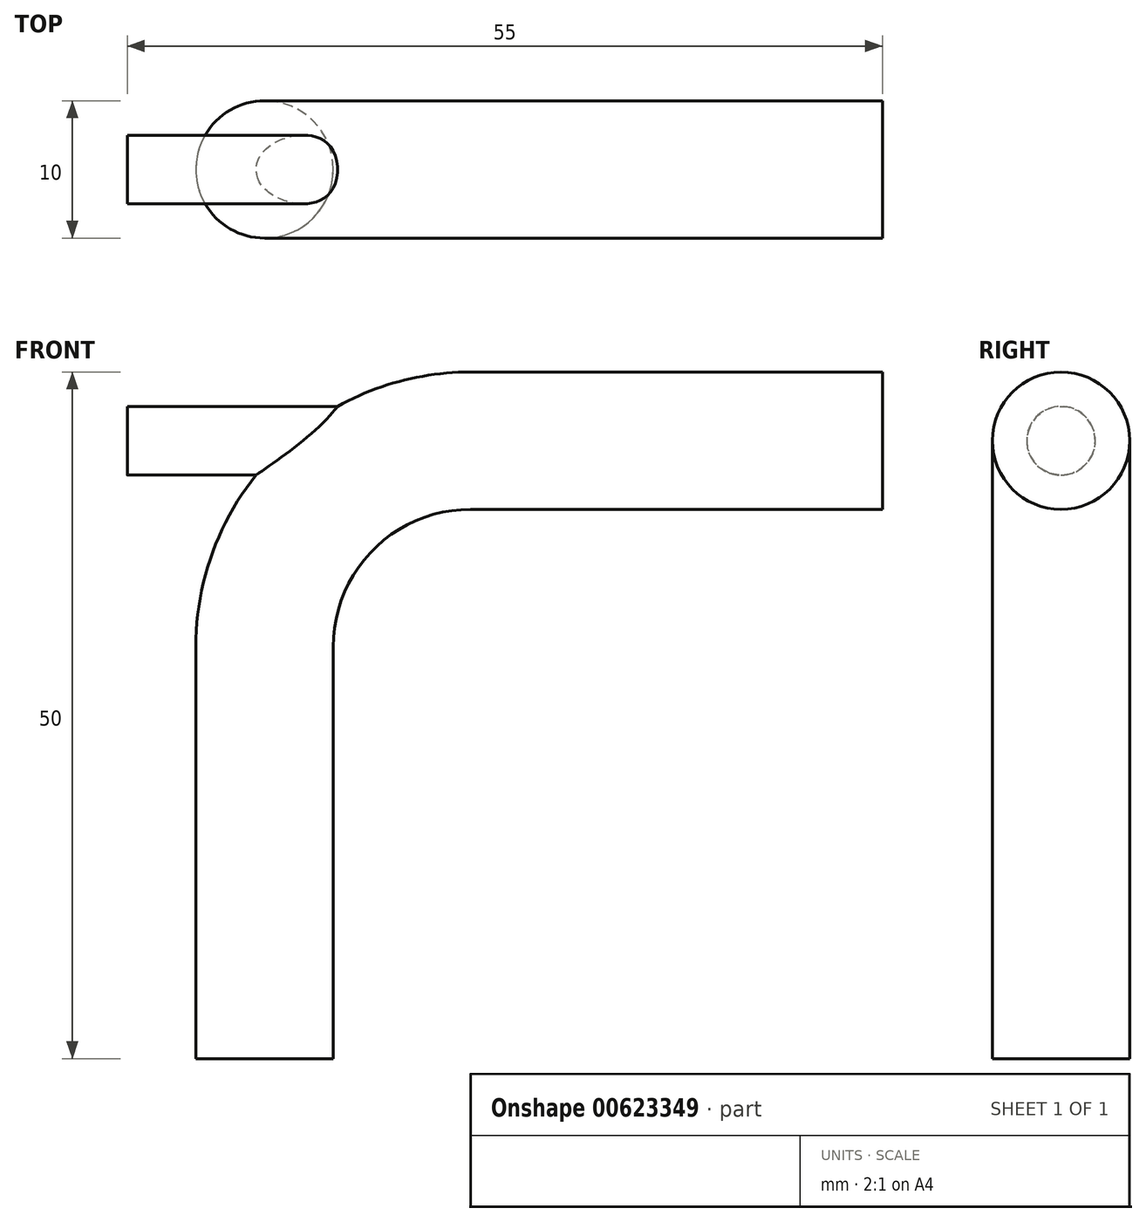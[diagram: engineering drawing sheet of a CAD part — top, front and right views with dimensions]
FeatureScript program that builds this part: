
annotation { "Feature Type Name" : "Feature", "Feature Type Description" : "" }
export const myFeature = defineFeature(function(context is Context, id is Id, definition is map)
    precondition{}
    {
        {
            var Q0;
            Q0=qCreatedBy(makeId("Front.planeOp"),FACE);
            var sketch = newSketch(context, id + "F0", { "sketchPlane" : qUnion([Q0])});
            skLineSegment(sketch, "E0", {"start": v(0, 0) * mm, "end": v(0, 30) * mm});
            skArc(sketch, "E1", {"start": v(15, 45) * mm, "mid": v(4.4, 40.6) * mm, "end": v(0, 30) * mm});
            skLineSegment(sketch, "E2", {"start": v(15, 45) * mm, "end": v(45, 45) * mm});
            skSolve(sketch);
        }
        {
            var Q0;
            Q0=qCreatedBy(makeId("Top.planeOp"),FACE);
            var sketch = newSketch(context, id + "F1", { "sketchPlane" : qUnion([Q0])});
            skCircle(sketch, "E3", {"center": v(0, 0) * mm, "radius": 5 * mm});
            skSolve(sketch);
        }
        {
            var Q0;
            Q0 = qSketchRegion(id + "F1", true);
            var Q1;
            Q1 = qConstructionFilter(qBodyType(qCreatedBy(id + "F0" ,EDGE), BodyType.WIRE), ConstructionObject.NO);
            sweep(context, id + "F2", {"profiles" : qUnion([Q0]), "path" : qUnion([Q1])});
        }
        {
            var Q0;
            Q0=qCreatedBy(makeId("Right.planeOp"),FACE);
            cPlane(context, id + "F3", {"entities" : qUnion([Q0]), "cplaneType" : CPlaneType.OFFSET, "offset" : 10 * mm, "oppositeDirection" : true, "width" : 150 * mm, "height" : 150 * mm});
        }
        {
            var Q0;
            Q0=qCreatedBy(id+"F3.planeOp",FACE);
            var sketch = newSketch(context, id + "F4", { "sketchPlane" : qUnion([Q0])});
            skCircle(sketch, "E4", {"center": v(0, 45) * mm, "radius": 2.5 * mm});
            skSolve(sketch);
        }
        {
            var Q0;
            Q0=makeQuery(id+"F4.imprint","IMPRINT",FACE,{"disambiguationData":[TD([[makeQuery(id+"F4.imprint","IMPRINT",EDGE,{"derivedFrom":sQuery(id+"F4.wireOp",EDGE,"E4")}),1.0]])]});
            extrude(context, id + "F5", {"entities" : qUnion([Q0]), "operationType" : NewBodyOperationType.ADD, "depth" : 30 * mm, "offsetDistance" : 25 * mm});
        }
    });
